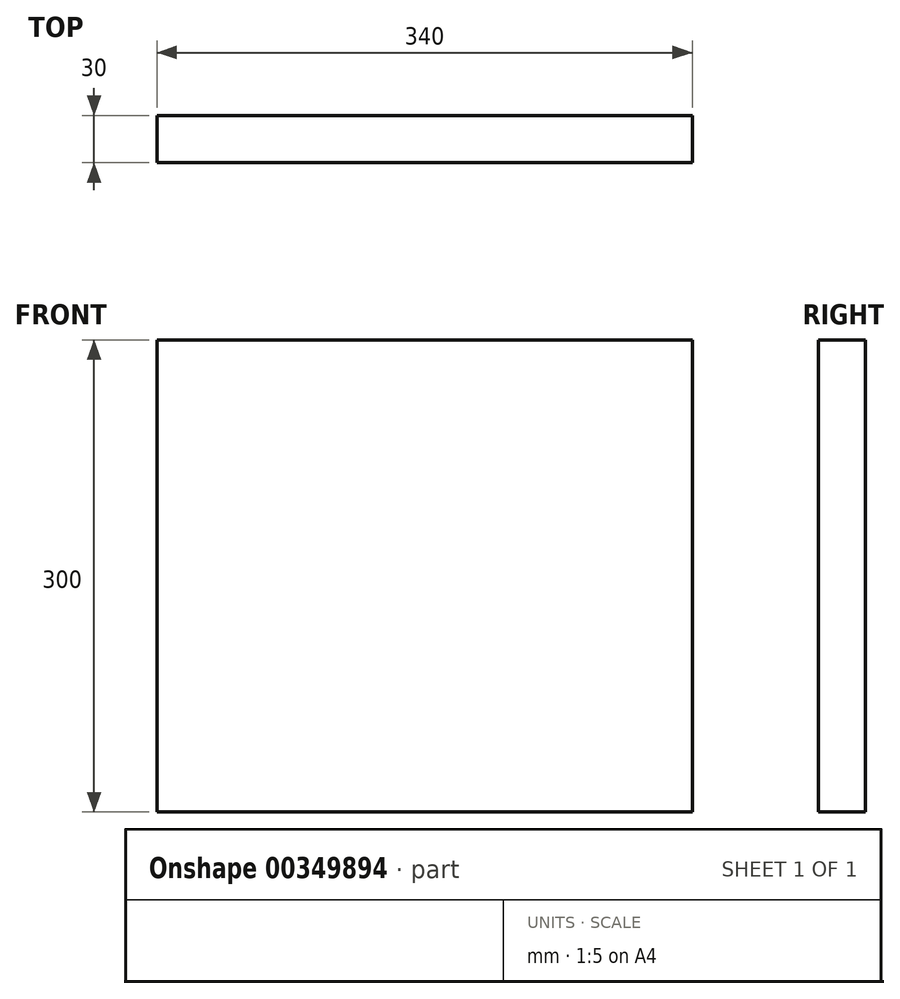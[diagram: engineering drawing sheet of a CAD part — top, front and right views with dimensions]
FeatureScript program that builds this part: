
annotation { "Feature Type Name" : "Feature", "Feature Type Description" : "" }
export const myFeature = defineFeature(function(context is Context, id is Id, definition is map)
    precondition{}
    {
        {
            var Q0;
            Q0=qCreatedBy(makeId("Front.planeOp"),FACE);
            var sketch = newSketch(context, id + "F0", { "sketchPlane" : qUnion([Q0])});
            skLineSegment(sketch, "E0.bottom", {"start": v(0, 0) * mm, "end": v(340, 0) * mm});
            skLineSegment(sketch, "E0.top", {"start": v(0, -300) * mm, "end": v(340, -300) * mm});
            skLineSegment(sketch, "E0.left", {"start": v(0, 0) * mm, "end": v(0, -300) * mm});
            skLineSegment(sketch, "E0.right", {"start": v(340, 0) * mm, "end": v(340, -300) * mm});
            skSolve(sketch);
        }
        {
            var Q0;
            Q0 = qSketchRegion(id + "F0", true);
            extrude(context, id + "F1", {"entities" : qUnion([Q0]), "depth" : 30 * mm});
        }
    });
